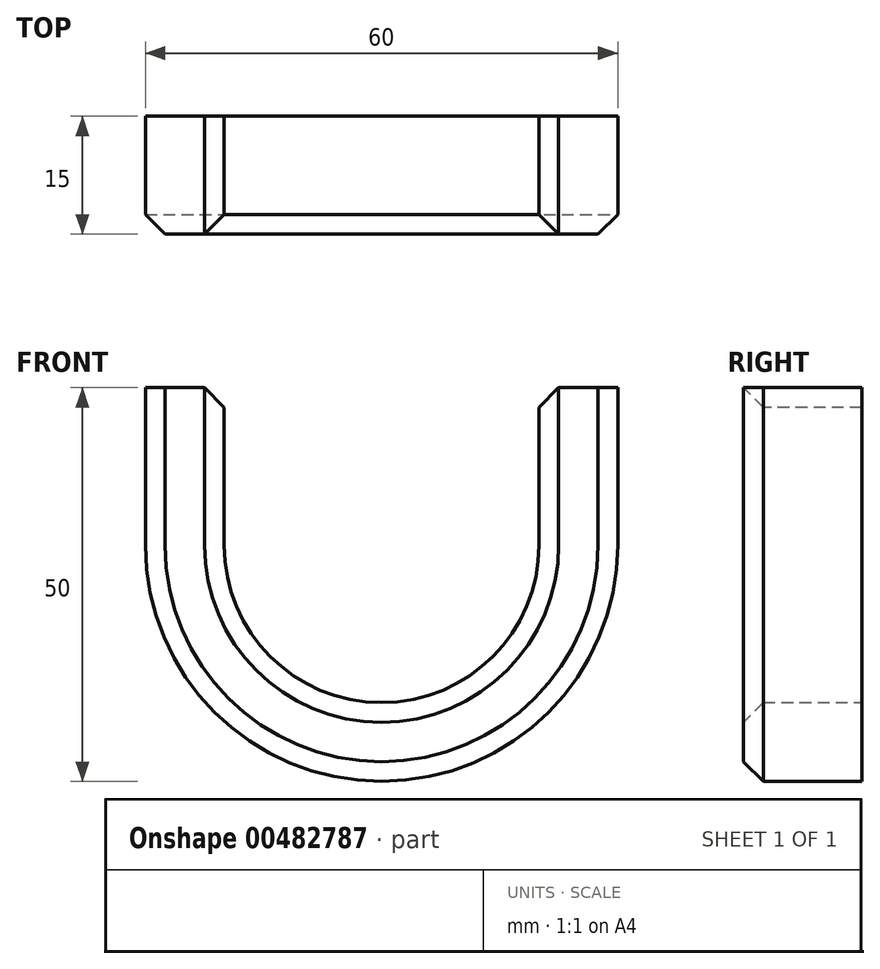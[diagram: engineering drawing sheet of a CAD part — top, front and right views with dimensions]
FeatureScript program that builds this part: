
annotation { "Feature Type Name" : "Feature", "Feature Type Description" : "" }
export const myFeature = defineFeature(function(context is Context, id is Id, definition is map)
    precondition{}
    {
        {
            var Q0;
            Q0=qCreatedBy(makeId("Front.planeOp"),FACE);
            var sketch = newSketch(context, id + "F0", { "sketchPlane" : qUnion([Q0])});
            skArc(sketch, "E0", {"start": v(-20, 0) * mm, "mid": v(0, -20) * mm, "end": v(20, 0) * mm});
            skLineSegment(sketch, "E1", {"start": v(20, 0) * mm, "end": v(20, 20) * mm});
            skLineSegment(sketch, "E2", {"start": v(-20, 0) * mm, "end": v(-20, 20) * mm});
            skLineSegment(sketch, "E3.0", {"start": v(-30, 0) * mm, "end": v(-30, 20) * mm});
            skArc(sketch, "E3.1", {"start": v(-30, 0) * mm, "mid": v(0, -30) * mm, "end": v(30, 0) * mm});
            skLineSegment(sketch, "E3.2", {"start": v(30, 0) * mm, "end": v(30, 20) * mm});
            skLineSegment(sketch, "E4", {"start": v(-30, 20) * mm, "end": v(-20, 20) * mm});
            skLineSegment(sketch, "E5", {"start": v(20, 20) * mm, "end": v(30, 20) * mm});
            skSolve(sketch);
        }
        {
            var Q0;
            Q0=makeQuery(id+"F0.imprint","IMPRINT",FACE,{"disambiguationData":[TD([[makeQuery(id+"F0.imprint","IMPRINT",EDGE,{"derivedFrom":sQuery(id+"F0.wireOp",EDGE,"E0")}),-1.0]])]});
            extrude(context, id + "F1", {"entities" : qUnion([Q0]), "depth" : 15 * mm});
        }
        {
            var Q0;
            Q0=makeQuery(id+"F1.opExtrude","SWEPT_EDGE",EDGE,{"disambiguationData":[OSD([sQuery(id+"F0.wireOp",EDGE,"E1"),sQuery(id+"F0.wireOp",EDGE,"E5")])]});
            var Q1;
            Q1=makeQuery(id+"F1.opExtrude","SWEPT_EDGE",EDGE,{"disambiguationData":[OSD([sQuery(id+"F0.wireOp",EDGE,"E2"),sQuery(id+"F0.wireOp",EDGE,"E4")])]});
            var Q2;
            Q2=makeQuery(id+"F1.opExtrude","CAP_EDGE",EDGE,{"disambiguationData":[OSD([sQuery(id+"F0.wireOp",EDGE,"E3.2")])],"isStart":false});
            var Q3;
            Q3=makeQuery(id+"F1.opExtrude","CAP_EDGE",EDGE,{"disambiguationData":[OSD([sQuery(id+"F0.wireOp",EDGE,"E2")])],"isStart":false});
            chamfer(context, id + "F2", {"entities" : qUnion([Q0, Q1, Q2, Q3]), "width" : 2.5 * mm, "tangentPropagation" : true});
        }
    });
